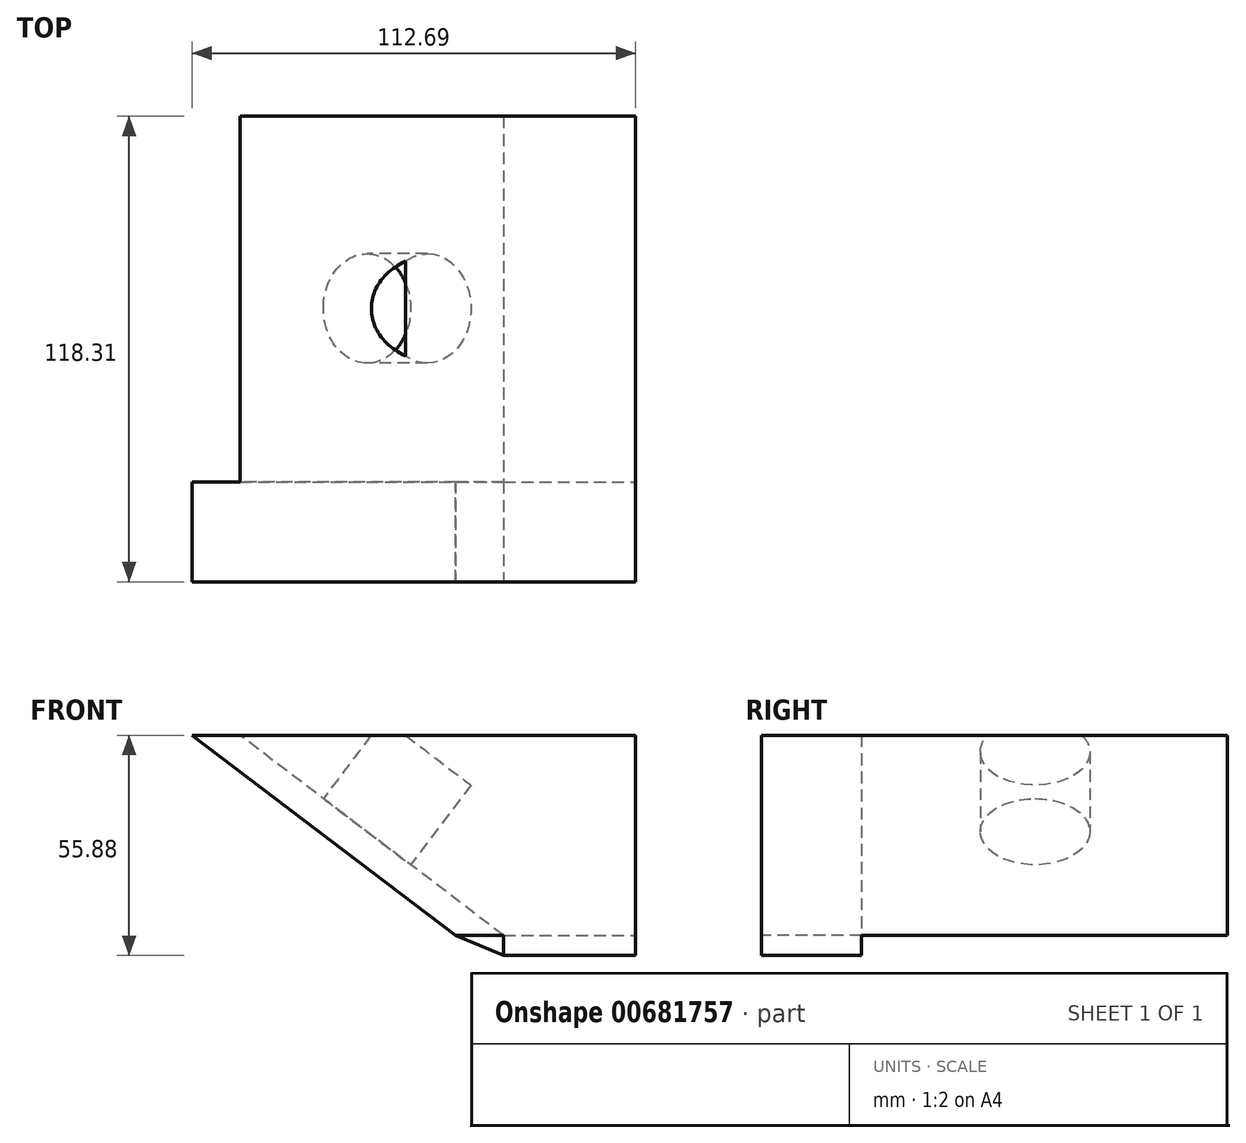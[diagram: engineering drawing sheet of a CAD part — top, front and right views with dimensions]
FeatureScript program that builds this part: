
annotation { "Feature Type Name" : "Feature", "Feature Type Description" : "" }
export const myFeature = defineFeature(function(context is Context, id is Id, definition is map)
    precondition{}
    {
        {
            var Q0;
            Q0=qCreatedBy(makeId("Top.planeOp"),FACE);
            var sketch = newSketch(context, id + "F0", { "sketchPlane" : qUnion([Q0])});
            skLineSegment(sketch, "E0.bottom", {"start": v(-62.63, 48.86) * mm, "end": v(70.64, 48.86) * mm});
            skLineSegment(sketch, "E0.top", {"start": v(-62.63, -44.05) * mm, "end": v(70.64, -44.05) * mm});
            skLineSegment(sketch, "E0.left", {"start": v(-62.63, 48.86) * mm, "end": v(-62.63, -44.05) * mm});
            skLineSegment(sketch, "E0.right", {"start": v(70.64, 48.86) * mm, "end": v(70.64, -44.05) * mm});
            skSolve(sketch);
        }
        {
            var Q0;
            Q0=makeQuery(id+"F0.imprint","IMPRINT",FACE,{"disambiguationData":[TD([[makeQuery(id+"F0.imprint","IMPRINT",EDGE,{"derivedFrom":sQuery(id+"F0.wireOp",EDGE,"E0.bottom")}),-1.0]])]});
            extrude(context, id + "F1", {"entities" : qUnion([Q0]), "depth" : 50.8 * mm, "offsetDistance" : 25.4 * mm});
        }
        {
            var Q0;
            Q0=makeQuery(id+"F1.opExtrude","SWEPT_FACE",FACE,{"disambiguationData":[OSD([sQuery(id+"F0.wireOp",EDGE,"E0.top")])]});
            var sketch = newSketch(context, id + "F2", { "sketchPlane" : qUnion([Q0])});
            skLineSegment(sketch, "E1", {"start": v(-29.87, 50.8) * mm, "end": v(37.08, 0) * mm});
            skLineSegment(sketch, "E2", {"start": v(37.08, 0) * mm, "end": v(-62.63, 0) * mm});
            skLineSegment(sketch, "E3", {"start": v(-62.63, 0) * mm, "end": v(-62.63, 50.8) * mm});
            skLineSegment(sketch, "E4", {"start": v(-62.63, 50.8) * mm, "end": v(-29.5, 50.14) * mm});
            skSolve(sketch);
        }
        {
            var Q0;
            {var subQ0=sQuery(id+"F2.wireOp",EDGE,"E1");Q0=makeQuery(id+"F2.imprint","IMPRINT",FACE,{"disambiguationData":[TD([[makeQuery(id+"F2.imprint","IMPRINT",EDGE,{"derivedFrom":subQ0}),-1.0]])]});}
            extrude(context, id + "F3", {"entities" : qUnion([Q0]), "operationType" : NewBodyOperationType.REMOVE, "oppositeDirection" : true, "depth" : 127 * mm, "offsetDistance" : 25.4 * mm});
        }
        {
            var Q0;
            Q0=makeQuery(id+"F1.opExtrude","SWEPT_FACE",FACE,{"disambiguationData":[OSD([sQuery(id+"F0.wireOp",EDGE,"E0.top")])]});
            var sketch = newSketch(context, id + "F4", { "sketchPlane" : qUnion([Q0])});
            skLineSegment(sketch, "E5", {"start": v(70.64, 50.8) * mm, "end": v(70.64, 0) * mm});
            skLineSegment(sketch, "E6", {"start": v(70.64, 0) * mm, "end": v(24.9, 0) * mm});
            skLineSegment(sketch, "E7", {"start": v(24.9, 0) * mm, "end": v(-42.05, 50.8) * mm});
            skLineSegment(sketch, "E8", {"start": v(-42.05, 50.8) * mm, "end": v(70.64, 50.8) * mm});
            skSolve(sketch);
        }
        {
            var Q0;
            {var subQ2=sQuery(id+"F4.wireOp",EDGE,"E7");Q0=makeQuery(id+"F4.imprint","IMPRINT",FACE,{"disambiguationData":[TD([[makeQuery(id+"F4.imprint","IMPRINT",EDGE,{"derivedFrom":subQ2}),-1.0]])]});}
            extrude(context, id + "F5", {"entities" : qUnion([Q0]), "depth" : 25.4 * mm, "offsetDistance" : 25.4 * mm});
        }
        {
            var Q0;
            Q0=makeQuery(id+"F1.opExtrude","SWEPT_FACE",FACE,{"disambiguationData":[OSD([sQuery(id+"F0.wireOp",EDGE,"E0.top")])]});
            extrude(context, id + "F6", {"entities" : qUnion([Q0]), "depth" : 25.4 * mm, "offsetDistance" : 25.4 * mm});
        }
        {
            var Q0;
            Q0=makeQuery(id+"F3.boolean.opBoolean","COPY",FACE,{"derivedFrom":makeQuery(id+"F3.opExtrude","SWEPT_FACE",FACE,{"disambiguationData":[OSD([sQuery(id+"F2.wireOp",EDGE,"E1")])]})});
            var sketch = newSketch(context, id + "F7", { "sketchPlane" : qUnion([Q0])});
            skCircle(sketch, "E9", {"center": v(-14.02, 0) * mm, "radius": 13.9 * mm});
            skSolve(sketch);
        }
        {
            var Q0;
            Q0=makeQuery(id+"F7.imprint","IMPRINT",FACE,{"disambiguationData":[TD([[makeQuery(id+"F7.imprint","IMPRINT",EDGE,{"derivedFrom":sQuery(id+"F7.wireOp",EDGE,"E9")}),1.0]])]});
            extrude(context, id + "F8", {"entities" : qUnion([Q0]), "operationType" : NewBodyOperationType.REMOVE, "oppositeDirection" : true, "depth" : 25.4 * mm, "offsetDistance" : 25.4 * mm});
        }
        {
            var Q0;
            {var subQ0=sQuery(id+"F0.wireOp",EDGE,"E0.top");Q0=makeQuery(id+"F6.opExtrude","SWEPT_FACE",FACE,{"disambiguationData":[OSD([subQ0]),TDD([makeQuery(id+"F1.opExtrude","CAP_EDGE",EDGE,{"disambiguationData":[OSD([subQ0])],"isStart":true})])]});}
            var sketch = newSketch(context, id + "F9", { "sketchPlane" : qUnion([Q0])});
            skLineSegment(sketch, "E10", {"start": v(70.64, 69.45) * mm, "end": v(70.64, 44.05) * mm});
            skLineSegment(sketch, "E11", {"start": v(70.64, 44.05) * mm, "end": v(37.08, 44.05) * mm});
            skLineSegment(sketch, "E12", {"start": v(37.08, 44.05) * mm, "end": v(37.08, 69.45) * mm});
            skLineSegment(sketch, "E13", {"start": v(37.08, 69.45) * mm, "end": v(70.64, 69.45) * mm});
            skSolve(sketch);
        }
        {
            var Q0;
            Q0=makeQuery(id+"F9.imprint","IMPRINT",FACE,{"disambiguationData":[TD([[makeQuery(id+"F9.imprint","IMPRINT",EDGE,{"derivedFrom":sQuery(id+"F9.wireOp",EDGE,"E10")}),-1.0]])]});
            extrude(context, id + "F10", {"entities" : qUnion([Q0]), "operationType" : NewBodyOperationType.ADD, "depth" : 5.08 * mm, "offsetDistance" : 25.4 * mm});
        }
        {
            var Q0;
            Q0=makeQuery(id+"F10.boolean.opBoolean","MERGE",FACE,{"derivedFrom":[makeQuery(id+"F6.opExtrude","CAP_FACE",FACE,{"disambiguationData":[OSD([sQuery(id+"F0.wireOp",EDGE,"E0.top")])],"isStart":false}),makeQuery(id+"F10.opExtrude","SWEPT_FACE",FACE,{"disambiguationData":[OSD([sQuery(id+"F9.wireOp",EDGE,"E13")])]})]});
            var sketch = newSketch(context, id + "F11", { "sketchPlane" : qUnion([Q0])});
            skLineSegment(sketch, "E14", {"start": v(24.9, 0) * mm, "end": v(37.08, -5.08) * mm});
            skLineSegment(sketch, "E15", {"start": v(37.08, -5.08) * mm, "end": v(37.08, 0) * mm});
            skLineSegment(sketch, "E16", {"start": v(37.08, 0) * mm, "end": v(24.9, 0) * mm});
            skSolve(sketch);
        }
        {
            var Q0;
            Q0=makeQuery(id+"F11.imprint","IMPRINT",FACE,{"disambiguationData":[TD([[makeQuery(id+"F11.imprint","IMPRINT",EDGE,{"derivedFrom":sQuery(id+"F11.wireOp",EDGE,"E14")}),1.0]])]});
            extrude(context, id + "F12", {"entities" : qUnion([Q0]), "oppositeDirection" : true, "depth" : 25.4 * mm, "offsetDistance" : 25.4 * mm});
        }
    });
